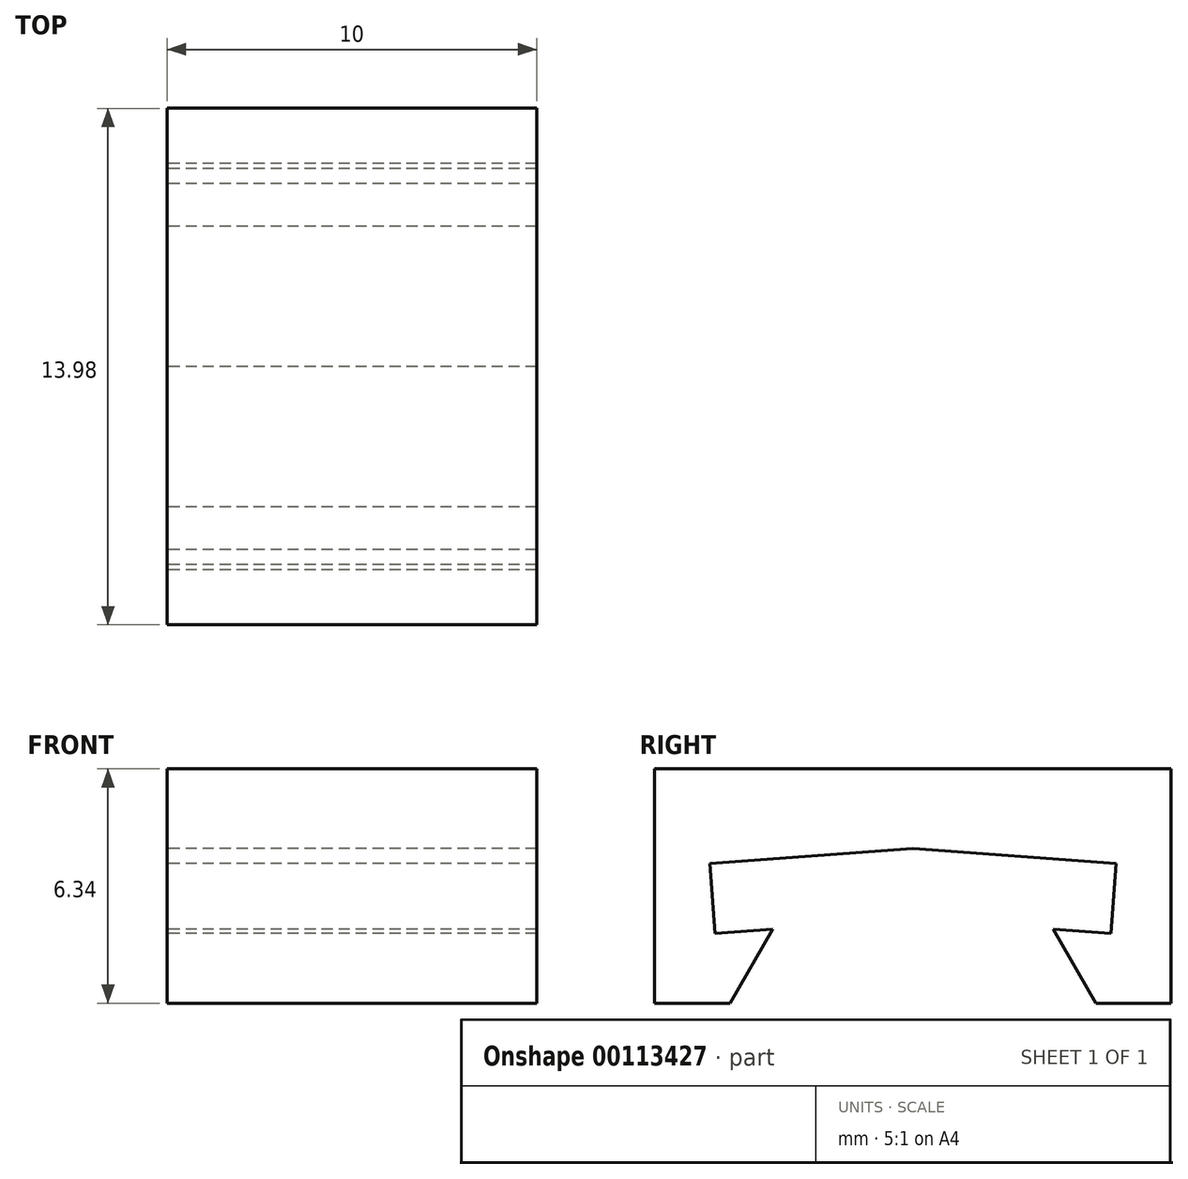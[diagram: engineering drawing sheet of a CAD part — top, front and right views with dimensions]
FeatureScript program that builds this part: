
annotation { "Feature Type Name" : "Feature", "Feature Type Description" : "" }
export const myFeature = defineFeature(function(context is Context, id is Id, definition is map)
    precondition{}
    {
        {
            var Q0;
            Q0=qCreatedBy(makeId("Right.planeOp"),FACE);
            var sketch = newSketch(context, id + "F0", { "sketchPlane" : qUnion([Q0])});
            skLineSegment(sketch, "E0", {"start": v(-7, 0) * mm, "end": v(-3.8, 0) * mm, "construction": true});
            skLineSegment(sketch, "E1", {"start": v(-3.8, 0) * mm, "end": v(-3.8, 2) * mm, "construction": true});
            skLineSegment(sketch, "E2", {"start": v(-3.8, 2) * mm, "end": v(-5, 2) * mm, "construction": true});
            skLineSegment(sketch, "E3", {"start": v(-5, 2) * mm, "end": v(-5, 3.8) * mm, "construction": true});
            skLineSegment(sketch, "E4", {"start": v(-5, 3.8) * mm, "end": v(0, 3.8) * mm, "construction": true});
            skLineSegment(sketch, "E5.MirrorCS", {"start": v(7, 0) * mm, "end": v(3.8, 0) * mm, "construction": true});
            skLineSegment(sketch, "E6.MirrorCS", {"start": v(3.8, 2) * mm, "end": v(5, 2) * mm, "construction": true});
            skLineSegment(sketch, "E7.MirrorCS", {"start": v(5, 3.8) * mm, "end": v(0, 3.8) * mm, "construction": true});
            skLineSegment(sketch, "E8.MirrorCS", {"start": v(3.8, 0) * mm, "end": v(3.8, 2) * mm, "construction": true});
            skLineSegment(sketch, "E9.MirrorCS", {"start": v(5, 2) * mm, "end": v(5, 3.8) * mm, "construction": true});
            skSolve(sketch);
        }
        {
            var Q0;
            Q0=qCreatedBy(makeId("Right.planeOp"),FACE);
            var sketch = newSketch(context, id + "F1", { "sketchPlane" : qUnion([Q0])});
            skLineSegment(sketch, "E10", {"start": v(-3.8, 2) * mm, "end": v(-4.95, 0) * mm});
            skLineSegment(sketch, "E11", {"start": v(-4.95, 0) * mm, "end": v(-7, 0) * mm});
            skLineSegment(sketch, "E12", {"start": v(-7, 0) * mm, "end": v(-7, 6) * mm});
            skLineSegment(sketch, "E13", {"start": v(-7, 6) * mm, "end": v(0, 6.34) * mm});
            skLineSegment(sketch, "E14", {"start": v(0, 6.34) * mm, "end": v(0, 4.19) * mm});
            skLineSegment(sketch, "E15", {"start": v(0, 4.19) * mm, "end": v(-5.5, 3.78) * mm});
            skLineSegment(sketch, "E16", {"start": v(-5.5, 3.78) * mm, "end": v(-5.36, 1.88) * mm});
            skLineSegment(sketch, "E17", {"start": v(-5.36, 1.88) * mm, "end": v(-3.8, 2) * mm});
            skLineSegment(sketch, "E18.MirrorCS", {"start": v(5.36, 1.88) * mm, "end": v(3.8, 2) * mm});
            skLineSegment(sketch, "E19.MirrorCS", {"start": v(7, 6) * mm, "end": v(0, 6.34) * mm});
            skLineSegment(sketch, "E20.MirrorCS", {"start": v(5.5, 3.78) * mm, "end": v(5.36, 1.88) * mm});
            skLineSegment(sketch, "E21.MirrorCS", {"start": v(3.8, 2) * mm, "end": v(4.95, 0) * mm});
            skLineSegment(sketch, "E22.MirrorCS", {"start": v(7, 0) * mm, "end": v(7, 6) * mm});
            skLineSegment(sketch, "E23.MirrorCS", {"start": v(4.95, 0) * mm, "end": v(7, 0) * mm});
            skLineSegment(sketch, "E24.MirrorCS", {"start": v(0, 4.19) * mm, "end": v(5.5, 3.78) * mm});
            skLineSegment(sketch, "E25.bottom", {"start": v(-7, 6) * mm, "end": v(7, 6) * mm});
            skLineSegment(sketch, "E25.top", {"start": v(-7, 6.34) * mm, "end": v(7, 6.34) * mm});
            skLineSegment(sketch, "E25.left", {"start": v(-7, 6) * mm, "end": v(-7, 6.34) * mm});
            skLineSegment(sketch, "E25.right", {"start": v(7, 6) * mm, "end": v(7, 6.34) * mm});
            skSolve(sketch);
        }
        {
            var Q0;
            Q0 = qSketchRegion(id + "F1", true);
            extrude(context, id + "F2", {"entities" : qUnion([Q0]), "depth" : 10 * mm});
        }
    });
